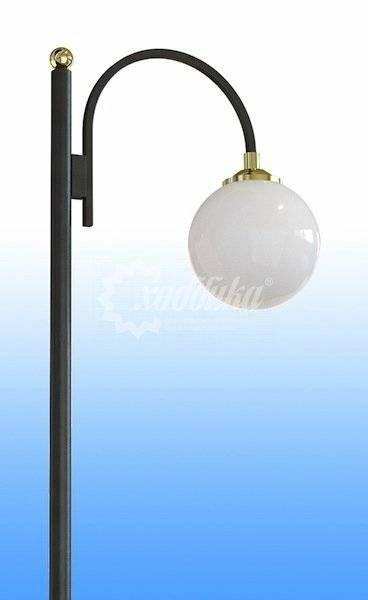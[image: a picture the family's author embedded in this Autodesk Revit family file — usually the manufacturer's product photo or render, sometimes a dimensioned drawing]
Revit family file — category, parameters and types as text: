
# Revit family: Стальной фонарный столб Т-05-1 со светильником Арт 6977
name_source: partatom
category: Антураж
revit_build: Autodesk Revit 2018 (Build: 20180423_1000(x64)
units: mm (PartAtom-declared; Revit-internal decimal feet)

## family parameters
Всегда вертикально = Да
Источник визуального образа = Геометрия семейства
На основе рабочей плоскости = Нет
Общий = Нет
При загрузке вырезать с полостями = Нет
Точка расчета площади = Нет

## types (6) — shared parameters
URL = https://hobbyka.ru
Артикул товара = Арт. 6977
Группа модели = Светильники со стальными опорами
Длина = 756 мм
Изготовитель = ООО «Хоббика»
Изображение типоразмера = Стальной фонарный столб Т-05-1 со светильником Арт 6977.jpg
Материал изделия = Сталь
Цвет каркаса = Сталь
Ширина = 400 мм

## per-type parameters (varying)
| type | Версия 3,26 м | Версия 3,76 м | Версия 4,26 м | Версия 4,76 м | Версия 5,26 м | Высота | Высота столба | Описание |
| Версия 3,26 м | Да | Нет | Нет | Нет | Нет | 3260 мм | 2560 мм | Стальной фонарный столб Т-05-1 со светильником. Модель 3,26 м |
| Версия 3,76 м | Нет | Да | Нет | Нет | Нет | 3760 мм | 3060 мм | Стальной фонарный столб Т-05-1 со светильником. Модель 3,76 м |
| Версия 4,26 м | Нет | Нет | Да | Нет | Нет | 4260 мм | 3560 мм | Стальной фонарный столб Т-05-1 со светильником. Модель 4,26 м |
| Версия 4,76 м | Нет | Нет | Нет | Да | Нет | 4760 мм | 4060 мм | Стальной фонарный столб Т-05-1 со светильником. Модель 4,76 м |
| Версия 5,26 м | Нет | Нет | Нет | Нет | Да | 5260 мм | 4560 мм | Стальной фонарный столб Т-05-1 со светильником. Модель 5,26 м |
| Версия 5,76 м | Нет | Нет | Нет | Нет | Нет | 5760 мм | 5060 мм | Стальной фонарный столб Т-05-1 со светильником. Модель 5,76 м |
